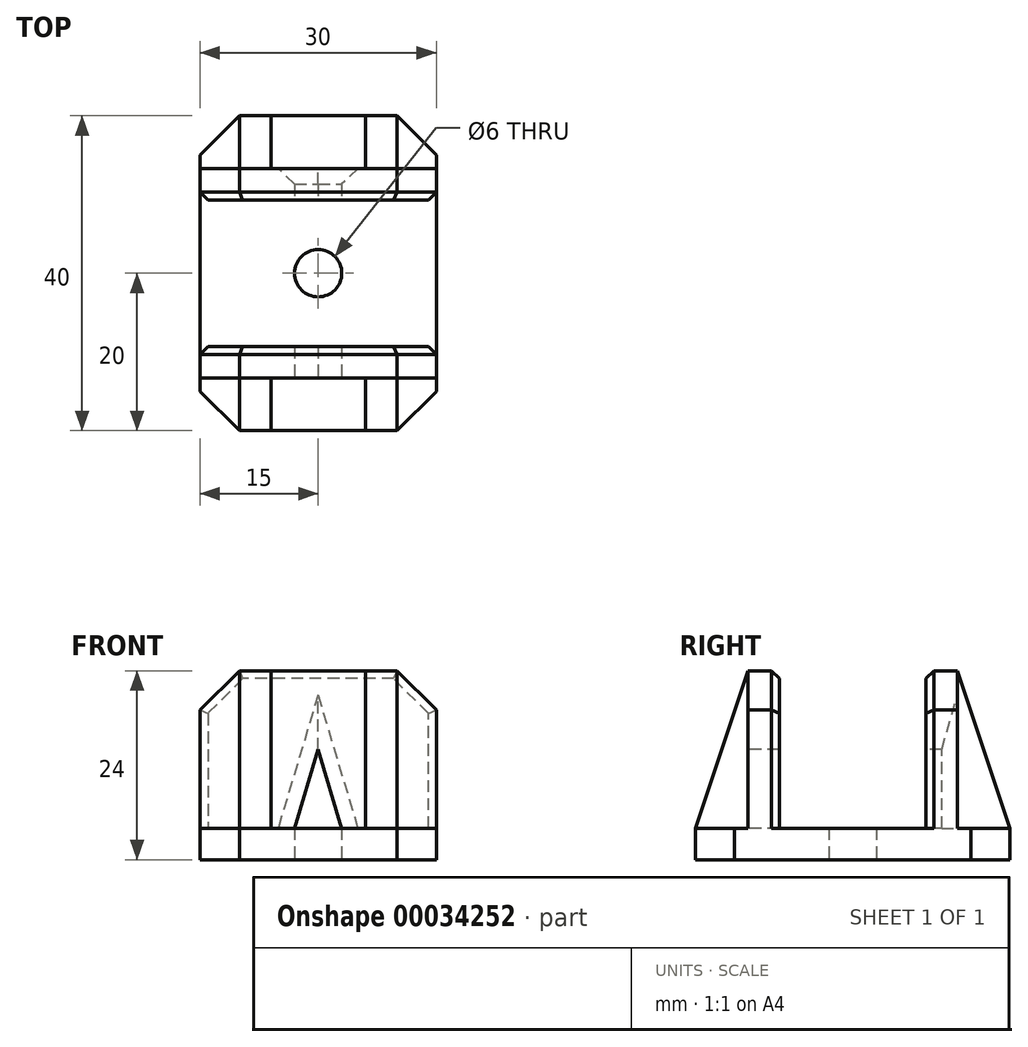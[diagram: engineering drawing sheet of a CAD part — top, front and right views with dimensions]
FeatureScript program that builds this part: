
annotation { "Feature Type Name" : "Feature", "Feature Type Description" : "" }
export const myFeature = defineFeature(function(context is Context, id is Id, definition is map)
    precondition{}
    {
        {
            var Q0;
            Q0=qCreatedBy(makeId("Top.planeOp"),FACE);
            var sketch = newSketch(context, id + "F0", { "sketchPlane" : qUnion([Q0])});
            skLineSegment(sketch, "E0.rect.bottom", {"start": v(15, -9.32) * mm, "end": v(-15, -9.32) * mm, "construction": true});
            skLineSegment(sketch, "E0.rect.top", {"start": v(15, 9.32) * mm, "end": v(-15, 9.32) * mm, "construction": true});
            skLineSegment(sketch, "E0.rect.left", {"start": v(15, -9.32) * mm, "end": v(15, 9.32) * mm, "construction": true});
            skLineSegment(sketch, "E0.rect.right", {"start": v(-15, -9.32) * mm, "end": v(-15, 9.32) * mm, "construction": true});
            skPoint(sketch, "E0.rect.middle", {"position": v(0, 0) * mm});
            skLineSegment(sketch, "E1.rect.bottom", {"start": v(15, 20) * mm, "end": v(-15, 20) * mm});
            skLineSegment(sketch, "E1.rect.top", {"start": v(15, -20) * mm, "end": v(-15, -20) * mm});
            skLineSegment(sketch, "E1.rect.left", {"start": v(15, 20) * mm, "end": v(15, -20) * mm});
            skLineSegment(sketch, "E1.rect.right", {"start": v(-15, 20) * mm, "end": v(-15, -20) * mm});
            skCircle(sketch, "E2", {"center": v(0, 0) * mm, "radius": 3 * mm});
            skSolve(sketch);
        }
        {
            var Q0;
            Q0 = qSketchRegion(id + "F0", true);
            extrude(context, id + "F1", {"entities" : qUnion([Q0]), "depth" : 4 * mm});
        }
        {
            var Q0;
            Q0=makeQuery(id+"F1.opExtrude","CAP_FACE",FACE,{"disambiguationData":[OSD([sQuery(id+"F0.wireOp",EDGE,"E1.rect.bottom"),sQuery(id+"F0.wireOp",EDGE,"E1.rect.top"),sQuery(id+"F0.wireOp",EDGE,"E1.rect.left"),sQuery(id+"F0.wireOp",EDGE,"E1.rect.right"),sQuery(id+"F0.wireOp",EDGE,"E2")])],"isStart":false});
            var sketch = newSketch(context, id + "F2", { "sketchPlane" : qUnion([Q0])});
            skLineSegment(sketch, "E3.rect.bottom", {"start": v(15, 9.32) * mm, "end": v(-15, 9.32) * mm});
            skLineSegment(sketch, "E3.rect.top", {"start": v(15, -9.32) * mm, "end": v(-15, -9.32) * mm});
            skLineSegment(sketch, "E3.rect.left", {"start": v(15, 9.32) * mm, "end": v(15, -9.32) * mm, "construction": true});
            skLineSegment(sketch, "E3.rect.right", {"start": v(-15, 9.32) * mm, "end": v(-15, -9.32) * mm, "construction": true});
            skPoint(sketch, "E3.rect.middle", {"position": v(0, 0) * mm});
            skLineSegment(sketch, "E4", {"start": v(-15, 9.32) * mm, "end": v(-15, 13.32) * mm});
            skLineSegment(sketch, "E5", {"start": v(-15, 13.32) * mm, "end": v(-10, 13.32) * mm});
            skLineSegment(sketch, "E6", {"start": v(-10, 13.32) * mm, "end": v(-10, 20) * mm});
            skLineSegment(sketch, "E7", {"start": v(-10, 20) * mm, "end": v(-6, 20) * mm});
            skLineSegment(sketch, "E8", {"start": v(-6, 20) * mm, "end": v(-6, 13.32) * mm});
            skLineSegment(sketch, "E9", {"start": v(-6, 13.32) * mm, "end": v(6, 13.32) * mm});
            skLineSegment(sketch, "E10", {"start": v(6, 13.32) * mm, "end": v(6, 20) * mm});
            skLineSegment(sketch, "E11", {"start": v(6, 20) * mm, "end": v(10, 20) * mm});
            skLineSegment(sketch, "E12", {"start": v(10, 20) * mm, "end": v(10, 13.32) * mm});
            skLineSegment(sketch, "E13", {"start": v(10, 13.32) * mm, "end": v(15, 13.32) * mm});
            skLineSegment(sketch, "E14", {"start": v(15, 13.32) * mm, "end": v(15, 9.32) * mm});
            skLineSegment(sketch, "E15", {"start": v(-15, -9.32) * mm, "end": v(-15, -13.32) * mm});
            skLineSegment(sketch, "E16", {"start": v(-15, -13.32) * mm, "end": v(-10, -13.32) * mm});
            skLineSegment(sketch, "E17", {"start": v(-10, -13.32) * mm, "end": v(-10, -20) * mm});
            skLineSegment(sketch, "E18", {"start": v(-10, -20) * mm, "end": v(-6, -20) * mm});
            skLineSegment(sketch, "E19", {"start": v(-6, -20) * mm, "end": v(-6, -13.32) * mm});
            skLineSegment(sketch, "E20", {"start": v(-6, -13.32) * mm, "end": v(6, -13.32) * mm});
            skLineSegment(sketch, "E21", {"start": v(6, -13.32) * mm, "end": v(6, -20) * mm});
            skLineSegment(sketch, "E22", {"start": v(6, -20) * mm, "end": v(10, -20) * mm});
            skLineSegment(sketch, "E23", {"start": v(10, -20) * mm, "end": v(10, -13.32) * mm});
            skLineSegment(sketch, "E24", {"start": v(10, -13.32) * mm, "end": v(15, -13.32) * mm});
            skLineSegment(sketch, "E25", {"start": v(15, -13.32) * mm, "end": v(15, -9.32) * mm});
            skSolve(sketch);
        }
        {
            var Q0;
            Q0 = qSketchRegion(id + "F2", true);
            extrude(context, id + "F3", {"entities" : qUnion([Q0]), "operationType" : NewBodyOperationType.ADD, "depth" : 20 * mm});
        }
        {
            var Q0;
            Q0=makeQuery(id+"F3.boolean.opBoolean","MERGE",FACE,{"derivedFrom":[makeQuery(id+"F1.opExtrude","SWEPT_FACE",FACE,{"disambiguationData":[OSD([sQuery(id+"F0.wireOp",EDGE,"E1.rect.right")])]}),makeQuery(id+"F3.opExtrude","SWEPT_FACE",FACE,{"disambiguationData":[OSD([sQuery(id+"F2.wireOp",EDGE,"E4")])]}),makeQuery(id+"F3.opExtrude","SWEPT_FACE",FACE,{"disambiguationData":[OSD([sQuery(id+"F2.wireOp",EDGE,"E15")])]})]});
            var sketch = newSketch(context, id + "F4", { "sketchPlane" : qUnion([Q0])});
            skLineSegment(sketch, "E26", {"start": v(-20, 4) * mm, "end": v(-13.32, 24) * mm});
            skLineSegment(sketch, "E27", {"start": v(-13.32, 24) * mm, "end": v(-20, 24) * mm});
            skLineSegment(sketch, "E28", {"start": v(-20, 24) * mm, "end": v(-20, 4) * mm});
            skLineSegment(sketch, "E29", {"start": v(13.32, 24) * mm, "end": v(20, 4) * mm});
            skLineSegment(sketch, "E30", {"start": v(20, 4) * mm, "end": v(20, 24) * mm});
            skLineSegment(sketch, "E31", {"start": v(20, 24) * mm, "end": v(13.32, 24) * mm});
            skSolve(sketch);
        }
        {
            var Q0;
            Q0 = qSketchRegion(id + "F4", true);
            extrude(context, id + "F5", {"entities" : qUnion([Q0]), "operationType" : NewBodyOperationType.REMOVE, "endBound" : BoundingType.THROUGH_ALL, "oppositeDirection" : true, "depth" : 25 * mm});
        }
        {
            var Q0;
            Q0=makeQuery(id+"F1.opExtrude","SWEPT_EDGE",EDGE,{"disambiguationData":[OSD([sQuery(id+"F0.wireOp",EDGE,"E1.rect.bottom"),sQuery(id+"F0.wireOp",EDGE,"E1.rect.right")])]});
            var Q1;
            Q1=makeQuery(id+"F1.opExtrude","SWEPT_EDGE",EDGE,{"disambiguationData":[OSD([sQuery(id+"F0.wireOp",EDGE,"E1.rect.top"),sQuery(id+"F0.wireOp",EDGE,"E1.rect.right")])]});
            var Q2;
            Q2=makeQuery(id+"F1.opExtrude","SWEPT_EDGE",EDGE,{"disambiguationData":[OSD([sQuery(id+"F0.wireOp",EDGE,"E1.rect.bottom"),sQuery(id+"F0.wireOp",EDGE,"E1.rect.left")])]});
            var Q3;
            Q3=makeQuery(id+"F1.opExtrude","SWEPT_EDGE",EDGE,{"disambiguationData":[OSD([sQuery(id+"F0.wireOp",EDGE,"E1.rect.top"),sQuery(id+"F0.wireOp",EDGE,"E1.rect.left")])]});
            var Q4;
            Q4=makeQuery(id+"F3.opExtrude","CAP_EDGE",EDGE,{"disambiguationData":[OSD([sQuery(id+"F2.wireOp",EDGE,"E4")])],"isStart":false});
            var Q5;
            Q5=makeQuery(id+"F3.opExtrude","CAP_EDGE",EDGE,{"disambiguationData":[OSD([sQuery(id+"F2.wireOp",EDGE,"E15")])],"isStart":false});
            var Q6;
            Q6=makeQuery(id+"F3.opExtrude","CAP_EDGE",EDGE,{"disambiguationData":[OSD([sQuery(id+"F2.wireOp",EDGE,"E25")])],"isStart":false});
            var Q7;
            Q7=makeQuery(id+"F3.opExtrude","CAP_EDGE",EDGE,{"disambiguationData":[OSD([sQuery(id+"F2.wireOp",EDGE,"E14")])],"isStart":false});
            chamfer(context, id + "F6", {"entities" : qUnion([Q0, Q1, Q2, Q3, Q4, Q5, Q6, Q7]), "width" : 5 * mm, "tangentPropagation" : true});
        }
        {
            var Q0;
            Q0=makeQuery(id+"F3.opExtrude","SWEPT_FACE",FACE,{"disambiguationData":[OSD([sQuery(id+"F2.wireOp",EDGE,"E20")])]});
            var sketch = newSketch(context, id + "F7", { "sketchPlane" : qUnion([Q0])});
            skLineSegment(sketch, "E32", {"start": v(-3, 4) * mm, "end": v(0, 14) * mm});
            skLineSegment(sketch, "E33", {"start": v(0, 14) * mm, "end": v(3, 4) * mm});
            skLineSegment(sketch, "E34", {"start": v(3, 4) * mm, "end": v(-3, 4) * mm});
            skSolve(sketch);
        }
        {
            var Q0;
            Q0 = qSketchRegion(id + "F7", true);
            extrude(context, id + "F8", {"entities" : qUnion([Q0]), "operationType" : NewBodyOperationType.REMOVE, "endBound" : BoundingType.THROUGH_ALL, "oppositeDirection" : true, "depth" : 25 * mm});
        }
        {
            var Q0;
            Q0=makeQuery(id+"F8.boolean.opBoolean","COPY",EDGE,{"derivedFrom":makeQuery(id+"F8.opExtrude","CAP_EDGE",EDGE,{"disambiguationData":[OSD([sQuery(id+"F7.wireOp",EDGE,"E32")])],"isStart":true})});
            var Q1;
            Q1=makeQuery(id+"F8.boolean.opBoolean","COPY",EDGE,{"derivedFrom":makeQuery(id+"F8.opExtrude","CAP_EDGE",EDGE,{"disambiguationData":[OSD([sQuery(id+"F7.wireOp",EDGE,"E33")])],"isStart":true})});
            var Q2;
            Q2=makeQuery(id+"F8.boolean.opBoolean","INTERSECT",EDGE,{"derivedFrom":[makeQuery(id+"F3.opExtrude","SWEPT_FACE",FACE,{"disambiguationData":[OSD([sQuery(id+"F2.wireOp",EDGE,"E9")])]}),makeQuery(id+"F8.opExtrude","SWEPT_FACE",FACE,{"disambiguationData":[OSD([sQuery(id+"F7.wireOp",EDGE,"E33")])]})]});
            var Q3;
            Q3=makeQuery(id+"F8.boolean.opBoolean","INTERSECT",EDGE,{"derivedFrom":[makeQuery(id+"F3.opExtrude","SWEPT_FACE",FACE,{"disambiguationData":[OSD([sQuery(id+"F2.wireOp",EDGE,"E9")])]}),makeQuery(id+"F8.opExtrude","SWEPT_FACE",FACE,{"disambiguationData":[OSD([sQuery(id+"F7.wireOp",EDGE,"E32")])]})]});
            chamfer(context, id + "F9", {"entities" : qUnion([Q0, Q1, Q2, Q3]), "chamferType" : ChamferType.OFFSET_ANGLE, "width" : 2 * mm, "oppositeDirection" : false, "angle" : 45 * degree, "tangentPropagation" : true});
        }
        {
            var Q0;
            Q0=makeQuery(id+"F3.opExtrude","SWEPT_EDGE",EDGE,{"disambiguationData":[OSD([sQuery(id+"F0.wireOp",EDGE,"E1.rect.left"),sQuery(id+"F2.wireOp",EDGE,"E3.rect.top"),sQuery(id+"F2.wireOp",EDGE,"E25")])]});
            var Q1;
            Q1=makeQuery(id+"F6.opChamfer","BLEND_EDGE",EDGE,{"blendedFrom":[makeQuery(id+"F3.opExtrude","CAP_EDGE",EDGE,{"disambiguationData":[OSD([sQuery(id+"F2.wireOp",EDGE,"E25")])],"isStart":false}),makeQuery(id+"F3.opExtrude","SWEPT_FACE",FACE,{"disambiguationData":[OSD([sQuery(id+"F2.wireOp",EDGE,"E3.rect.top")])]})],"blendedInto":[makeQuery(id+"F3.opExtrude","SWEPT_FACE",FACE,{"disambiguationData":[OSD([sQuery(id+"F2.wireOp",EDGE,"E3.rect.top")])]})]});
            var Q2;
            Q2=makeQuery(id+"F3.opExtrude","CAP_EDGE",EDGE,{"disambiguationData":[OSD([sQuery(id+"F2.wireOp",EDGE,"E3.rect.top")])],"isStart":false});
            var Q3;
            Q3=makeQuery(id+"F3.opExtrude","SWEPT_EDGE",EDGE,{"disambiguationData":[OSD([sQuery(id+"F0.wireOp",EDGE,"E1.rect.right"),sQuery(id+"F2.wireOp",EDGE,"E3.rect.top"),sQuery(id+"F2.wireOp",EDGE,"E15")])]});
            var Q4;
            Q4=makeQuery(id+"F6.opChamfer","BLEND_EDGE",EDGE,{"blendedFrom":[makeQuery(id+"F3.opExtrude","CAP_EDGE",EDGE,{"disambiguationData":[OSD([sQuery(id+"F2.wireOp",EDGE,"E15")])],"isStart":false}),makeQuery(id+"F3.opExtrude","SWEPT_FACE",FACE,{"disambiguationData":[OSD([sQuery(id+"F2.wireOp",EDGE,"E3.rect.top")])]})],"blendedInto":[makeQuery(id+"F3.opExtrude","SWEPT_FACE",FACE,{"disambiguationData":[OSD([sQuery(id+"F2.wireOp",EDGE,"E3.rect.top")])]})]});
            var Q5;
            Q5=makeQuery(id+"F3.opExtrude","SWEPT_EDGE",EDGE,{"disambiguationData":[OSD([sQuery(id+"F0.wireOp",EDGE,"E1.rect.right"),sQuery(id+"F2.wireOp",EDGE,"E3.rect.bottom"),sQuery(id+"F2.wireOp",EDGE,"E4")])]});
            var Q6;
            Q6=makeQuery(id+"F6.opChamfer","BLEND_EDGE",EDGE,{"blendedFrom":[makeQuery(id+"F3.opExtrude","CAP_EDGE",EDGE,{"disambiguationData":[OSD([sQuery(id+"F2.wireOp",EDGE,"E4")])],"isStart":false}),makeQuery(id+"F3.opExtrude","SWEPT_FACE",FACE,{"disambiguationData":[OSD([sQuery(id+"F2.wireOp",EDGE,"E3.rect.bottom")])]})],"blendedInto":[makeQuery(id+"F3.opExtrude","SWEPT_FACE",FACE,{"disambiguationData":[OSD([sQuery(id+"F2.wireOp",EDGE,"E3.rect.bottom")])]})]});
            var Q7;
            Q7=makeQuery(id+"F3.opExtrude","CAP_EDGE",EDGE,{"disambiguationData":[OSD([sQuery(id+"F2.wireOp",EDGE,"E3.rect.bottom")])],"isStart":false});
            var Q8;
            Q8=makeQuery(id+"F6.opChamfer","BLEND_EDGE",EDGE,{"blendedFrom":[makeQuery(id+"F3.opExtrude","CAP_EDGE",EDGE,{"disambiguationData":[OSD([sQuery(id+"F2.wireOp",EDGE,"E14")])],"isStart":false}),makeQuery(id+"F3.opExtrude","SWEPT_FACE",FACE,{"disambiguationData":[OSD([sQuery(id+"F2.wireOp",EDGE,"E3.rect.bottom")])]})],"blendedInto":[makeQuery(id+"F3.opExtrude","SWEPT_FACE",FACE,{"disambiguationData":[OSD([sQuery(id+"F2.wireOp",EDGE,"E3.rect.bottom")])]})]});
            var Q9;
            Q9=makeQuery(id+"F3.opExtrude","SWEPT_EDGE",EDGE,{"disambiguationData":[OSD([sQuery(id+"F0.wireOp",EDGE,"E1.rect.left"),sQuery(id+"F2.wireOp",EDGE,"E3.rect.bottom"),sQuery(id+"F2.wireOp",EDGE,"E14")])]});
            chamfer(context, id + "F10", {"entities" : qUnion([Q0, Q1, Q2, Q3, Q4, Q5, Q6, Q7, Q8, Q9]), "width" : 1 * mm, "tangentPropagation" : true});
        }
    });
